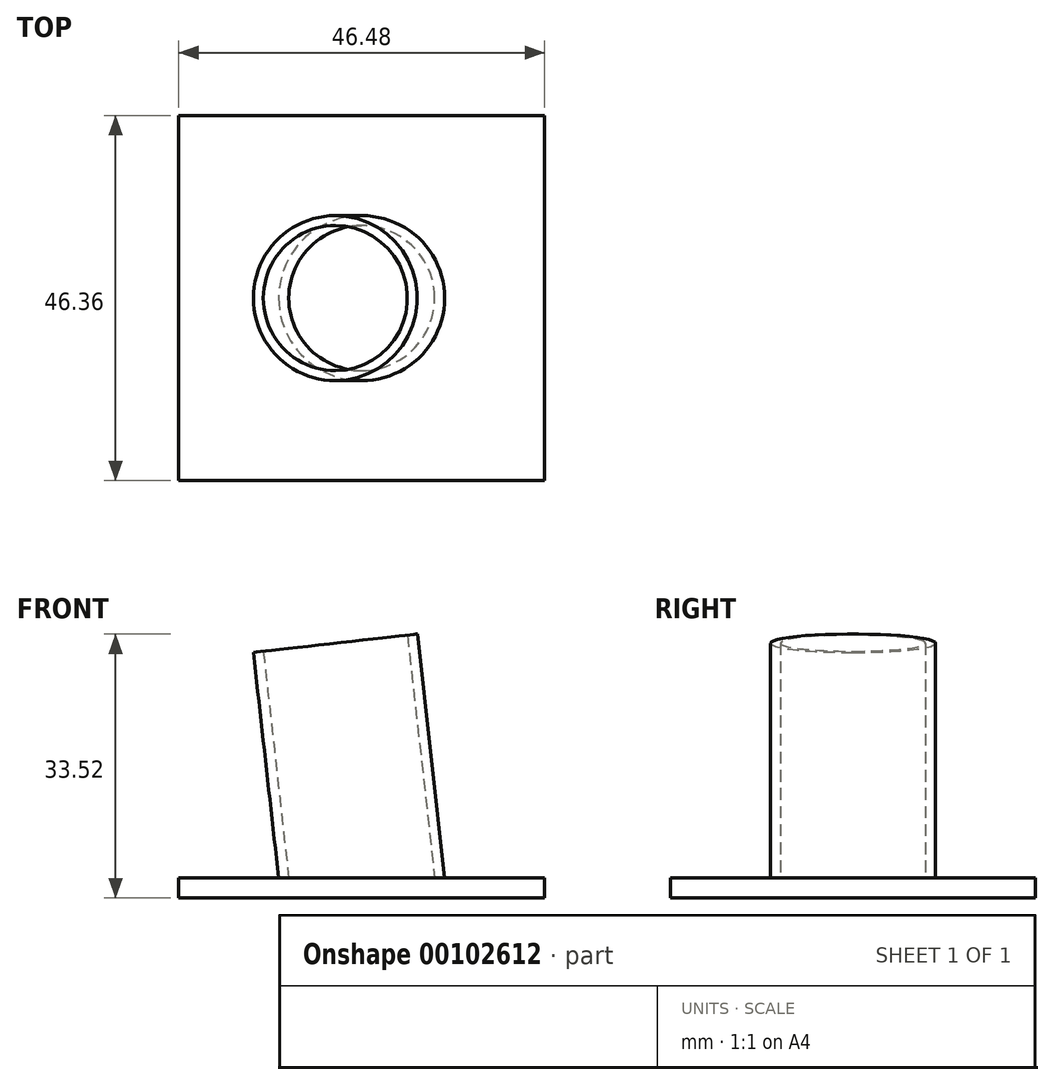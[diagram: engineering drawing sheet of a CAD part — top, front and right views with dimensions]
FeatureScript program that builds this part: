
annotation { "Feature Type Name" : "Feature", "Feature Type Description" : "" }
export const myFeature = defineFeature(function(context is Context, id is Id, definition is map)
    precondition{}
    {
        {
            var Q0;
            Q0=qCreatedBy(makeId("Top.planeOp"),FACE);
            var sketch = newSketch(context, id + "F0", { "sketchPlane" : qUnion([Q0])});
            skLineSegment(sketch, "E0", {"start": v(0, 75.88) * mm, "end": v(0, -75.68) * mm, "construction": true});
            skSolve(sketch);
        }
        {
            var Q0;
            Q0=sQuery(id+"F0.wireOp",EDGE,"E0");
            cPlane(context, id + "F1", {"entities" : qUnion([Q0]), "cplaneType" : CPlaneType.LINE_ANGLE, "offset" : 152.4 * mm, "angle" : 6.4 * degree, "width" : 152.4 * mm, "height" : 152.4 * mm});
        }
        {
            var Q0;
            Q0=qCreatedBy(id+"F1.planeOp",FACE);
            var sketch = newSketch(context, id + "F2", { "sketchPlane" : qUnion([Q0])});
            skCircle(sketch, "E1", {"center": v(41.03, 0) * mm, "radius": 9.2 * mm});
            skCircle(sketch, "E2", {"center": v(41.03, 0) * mm, "radius": 10.48 * mm});
            skSolve(sketch);
        }
        {
            var Q0;
            Q0=qSketchRegion(id+"F2",true);
            extrude(context, id + "F3", {"entities" : qUnion([Q0]), "oppositeDirection" : true, "depth" : 25.4 * mm});
        }
        {
            var Q0;
            Q0=makeQuery(id+"F3.opExtrude","CAP_FACE",FACE,{"disambiguationData":[OSD([sQuery(id+"F2.wireOp",EDGE,"E1"),sQuery(id+"F2.wireOp",EDGE,"E2")])],"isStart":true});
            extrude(context, id + "F4", {"entities" : qUnion([Q0]), "operationType" : NewBodyOperationType.ADD, "depth" : 25.4 * mm});
        }
        {
            var Q0;
            Q0=qCreatedBy(makeId("Front.planeOp"),FACE);
            var sketch = newSketch(context, id + "F5", { "sketchPlane" : qUnion([Q0])});
            skLineSegment(sketch, "E3.bottom", {"start": v(59.9, 0) * mm, "end": v(18.9, 0) * mm});
            skLineSegment(sketch, "E3.top", {"start": v(59.9, -25.69) * mm, "end": v(18.9, -25.69) * mm});
            skLineSegment(sketch, "E3.left", {"start": v(59.9, 0) * mm, "end": v(59.9, -25.69) * mm});
            skLineSegment(sketch, "E3.right", {"start": v(18.9, 0) * mm, "end": v(18.9, -25.69) * mm});
            skSolve(sketch);
        }
        {
            var Q0;
            Q0=qSketchRegion(id+"F5",true);
            extrude(context, id + "F6", {"entities" : qUnion([Q0]), "operationType" : NewBodyOperationType.REMOVE, "endBound" : BoundingType.SYMMETRIC, "oppositeDirection" : true, "depth" : 254 * mm});
        }
        {
            var Q0;
            Q0=qCreatedBy(makeId("Top.planeOp"),FACE);
            var sketch = newSketch(context, id + "F7", { "sketchPlane" : qUnion([Q0])});
            skLineSegment(sketch, "E4.bottom", {"start": v(18.05, 23.18) * mm, "end": v(64.53, 23.18) * mm});
            skLineSegment(sketch, "E4.top", {"start": v(18.05, -23.18) * mm, "end": v(64.53, -23.18) * mm});
            skLineSegment(sketch, "E4.left", {"start": v(18.05, 23.18) * mm, "end": v(18.05, -23.18) * mm});
            skLineSegment(sketch, "E4.right", {"start": v(64.53, 23.18) * mm, "end": v(64.53, -23.18) * mm});
            skLineSegment(sketch, "E5", {"start": v(51.83, 21.3) * mm, "end": v(51.83, -11.45) * mm, "construction": true});
            skLineSegment(sketch, "E6", {"start": v(23.5, -10.48) * mm, "end": v(51.74, -10.48) * mm, "construction": true});
            skLineSegment(sketch, "E7", {"start": v(30.75, -19.8) * mm, "end": v(30.75, 11.72) * mm, "construction": true});
            skSolve(sketch);
        }
        {
            var Q0;
            Q0=makeQuery(id+"F7.imprint","IMPRINT",FACE,{"disambiguationData":[TD([[makeQuery(id+"F7.imprint","IMPRINT",EDGE,{"derivedFrom":sQuery(id+"F7.wireOp",EDGE,"E4.bottom")}),-1.0]])]});
            extrude(context, id + "F8", {"entities" : qUnion([Q0]), "operationType" : NewBodyOperationType.ADD, "oppositeDirection" : true, "depth" : 2.54 * mm});
        }
    });
